# Revit family: Lighting-Accent-Acclaim-Flood One EO
name_source: partatom
category: Lighting Fixtures
revit_build: Autodesk Revit 2016 (Build: 20170117_1200(x64)
units: mm (PartAtom-declared; Revit-internal decimal feet)

## family parameters
Cut with Voids When Loaded = No
Host = Face
Light Source = Yes
Part Type = Normal
Room Calculation Point = No
Round Connector Dimension = Use Diameter
Shared = No

## types (1)
- Lighting-Accent-Acclaim-Flood One EO
    Apparent Load = 0 VA
    Color Filter = 16777215
    Default Elevation = 1219.2 mm  [stored 4 ft]
    Description = Floodlight
    Dimming Lamp Color Temperature Shift = <None>
    Emit Shape Visible in Rendering = No
    Emit from Rectangle Length = 270 mm  [stored 0.885827 ft]
    Emit from Rectangle Width = 145 mm  [stored 0.475722 ft]
    Housing Finish = Aluminum
    Lamp = LED
    Manufacturer = Acclaim Lighting
    Model = Flood One EO
    Number of Poles = 1
    Photometric Web File = generic
    Power Factor = 1
    Tilt Angle = -90.00°
    URL = http://www.acclaimlighting.com
    Voltage = 0 V
    Width = 321.06 mm

note: [stored X ft] marks values corroborated as IEEE doubles in the binary element streams (Revit-internal decimal feet)

## geometry (parser evidence)
native form markers: Blend x13, Sweep x3
no freeform markers — native parametric forms only
